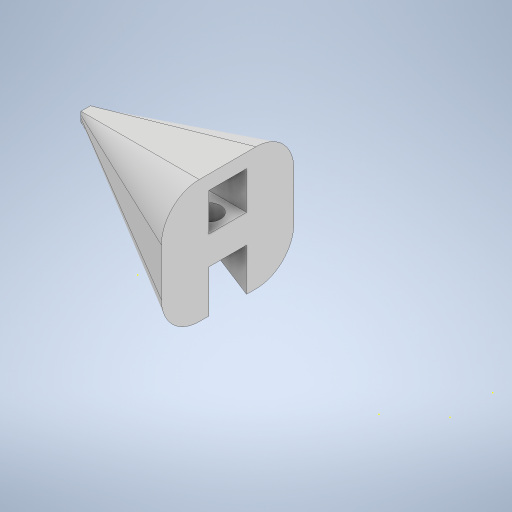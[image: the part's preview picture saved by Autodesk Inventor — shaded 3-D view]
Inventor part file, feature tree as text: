
AUTODESK INVENTOR PART (.ipt)
format: ipt  version: 2024 (Build 280153000, 153)  size: 766,464 bytes
history: native  units: mm
features: sketch x37, extrude x31, move_body x7, plane x5, split x5, boolean_combine x4, chamfer x3, fillet x1, loft x1, other x1
ambient origin geometry x8: Origin, YZ Plane, XZ Plane, XY Plane, X Axis, Y Axis, Z Axis, Center Point
bodies: Solid1 (feature_tree), Solid2 (feature_tree), Solid3 (feature_tree), Solid6 (feature_tree), Solid7 (feature_tree), Solid8 (feature_tree), Solid9 (feature_tree), Solid10 (feature_tree), Solid11 (feature_tree), Solid12 (feature_tree), Solid13 (feature_tree)
feature tree (95):
  extrude  "Extrusion1"  Depth=16.0mm
  sketch  "Sketch2"  dims[d2=15.0mm d3=0.0mm d4=10.0mm]
  extrude  "Extrusion2"  Depth=10.0mm
  chamfer  "Chamfer1"  Distance=21.25mm
  extrude  "Extrusion3"  Depth=10.0mm TaperAngle=0.0deg
  extrude  "Extrusion4"  Depth=11.5mm TaperAngle=0.0deg
  extrude  "Extrusion5"  Depth=1.0mm TaperAngle=0.0deg
  chamfer  "Chamfer2"  Distance=6.0mm Angle=45.0deg
  sketch  "Sketch6"  dims[d14=7.0mm d15=11.5mm d16=0.0mm]
  extrude  "Extrusion6"  Depth=9.0mm
  extrude  "Extrusion7"  Depth=5.5mm TaperAngle=0.0deg
  chamfer  "Chamfer3"  Distance=5.5mm Angle=45.0deg
  sketch  "Sketch9"  dims[d26=3.3mm d27=45.25mm d28=0.0mm d29=11.5mm d30=5.5mm d31=45.0deg]
  extrude  "Extrusion8"  Depth=65.75mm TaperAngle=0.0deg
  extrude  "Extrusion9"  Depth=9.0mm TaperAngle=0.0deg
  extrude  "Extrusion10"  Depth=13.0mm TaperAngle=0.0deg
  sketch  "Sketch13"  dims[d43=24.0mm d44=21.0mm d45=0.0mm]
  extrude  "Extrusion11"  Depth=21.0mm TaperAngle=0.0deg
  extrude  "Extrusion12"  TaperAngle=0.0deg  [1 undecoded]
  extrude  "Extrusion13"  Depth=6.0mm TaperAngle=0.0deg
  plane  "Work Plane1"
  split  "Split1"
  move_body  "Move Body1"
  extrude  "Extrusion14"  Depth=0.5mm TaperAngle=0.0deg
  move_body  "Move Body2"
  extrude  "Extrusion15"  Depth=3.0mm
  sketch  "Sketch19"  dims[d70=31.0mm d71=29.5mm d72=0.0mm]
  sketch  "Sketch20"  dims[d74=11.0mm d75=1.0mm]
  extrude  "Extrusion16"  Depth=10.0mm
  extrude  "Extrusion18"  Depth=29.5mm TaperAngle=0.0deg
  extrude  "Extrusion19"  Depth=1.0mm
  extrude  "Extrusion20"  Depth=10.0mm TaperAngle=0.0deg
  boolean_combine  "Combine1"
  plane  "Work Plane3"
  split  "Split3"
  extrude  "Extrusion21"  TaperAngle=0.0deg  [1 undecoded]
  plane  "Work Plane4"
  split  "Split4"
  move_body  "Move Body3"
  move_body  "Move Body4"
  boolean_combine  "Combine3"
  extrude  "Extrusion22"  Depth=1.0mm TaperAngle=0.0deg
  extrude  "Extrusion23"  Depth=12.5mm TaperAngle=0.0deg
  extrude  "Extrusion24"  TaperAngle=0.0deg  [1 undecoded]
  extrude  "Extrusion25"  Depth=46.5mm TaperAngle=0.0deg
  move_body  "Move Body5"
  sketch  "Sketch32"  dims[d102=46.5mm d103=0.0mm d104=4.0mm d105=1.0mm]
  boolean_combine  "Combine4"
  extrude  "Extrusion26"  Depth=2.0mm
  extrude  "Extrusion27"  Depth=4.0mm
  fillet  "Fillet2"  Radius=1.0mm
  sketch  "Sketch34"  dims[d109=5.5mm d110=4.0mm d111=0.0mm d112=0.0mm]
  extrude  "Extrusion28"  Depth=46.5mm TaperAngle=0.0deg
  plane  "Work Plane5"
  split  "Split5"
  move_body  "Move Body6"
  extrude  "Extrusion29"  Depth=4.0mm TaperAngle=0.0deg
  move_body  "Move Body7"
  boolean_combine  "Combine5"
  extrude  "Extrusion30"  TaperAngle=0.0deg  [1 undecoded]
  plane  "Work Plane6"
  loft  "Loft1"
  split  "Split6"
  extrude  "Extrusion31"  Depth=1.0mm
  extrude  "Extrusion32"  TaperAngle=0.0deg  [1 undecoded]
  sketch  "Sketch1"  dims[d0=36.0mm d1=16.0mm]
  sketch  "Sketch3"  dims[d5=10.0mm]
  sketch  "Sketch4"  dims[d6=3.3mm d7=21.25mm d8=0.0mm]
  sketch  "Sketch5"  dims[d9=10.0mm d10=5.5mm d11=45.0deg d12=10.0mm d13=0.0mm]
  sketch  "Sketch7"  dims[d17=3.3mm d18=1.0mm d19=0.0mm d20=6.0mm d21=11.5mm d22=45.0deg]
  sketch  "Sketch8"  dims[d23=15.0mm d24=0.0mm d25=9.0mm]
  sketch  "Sketch10"  dims[d32=2.0mm d33=65.75mm d34=0.0mm]
  sketch  "Sketch11"  dims[d35=0.5mm d36=0.0mm d37=9.0mm d38=0.0mm]
  sketch  "Sketch12"  dims[d39=0.5mm d40=0.0mm d41=13.0mm d42=0.0mm]
  sketch  "Sketch14"  dims[d46=12.25mm d47=-12.0mm d48=0.0mm d49=0.0mm]
  sketch  "Sketch15"  dims[d50=30.0mm d51=0.0mm d52=6.0mm d53=0.0mm d54=0.0mm]
  sketch  "Sketch16"  dims[d56=0.5mm d57=0.0mm d58=0.5mm d59=0.0mm]
  sketch  "Sketch17"  dims[d64=10.0mm d65=0.0mm d66=3.0mm]
  sketch  "Sketch18"  dims[d67=10.0mm d68=0.0mm d69=1.0mm]
  sketch  "Sketch22"  dims[d76=1.0mm d77=10.0mm d78=0.0mm]
  sketch  "Sketch25"  dims[d79=5.5mm d80=0.0mm d81=0.0mm d82=-1.0mm]
  sketch  "Sketch27"  dims[d83=0.0mm d84=0.0mm d85=1.0mm d86=1.0mm d87=0.0mm]
  sketch  "Sketch28"  dims[d88=1.0mm d89=0.0mm d90=12.5mm d91=0.0mm]
  sketch  "Sketch29"  dims[d92=19.0mm d93=0.0mm d94=-12.0mm d95=0.0mm d96=0.0mm]
  sketch  "Sketch30"  dims[d97=2.0mm d98=46.5mm d99=0.0mm]
  sketch  "Sketch31"  dims[d100=2.0mm d101=2.0mm]
  sketch  "Sketch33"  dims[d106=19.0mm d107=46.5mm d108=0.0mm]
  sketch  "Sketch35"  dims[d113=7.0mm d114=0.0mm d115=-8.0mm d116=0.0mm d117=0.0mm]
  sketch  "Sketch36"  dims[d118=7.0mm d119=19.75mm d120=0.0mm]
  sketch  "Sketch37"  dims[d121=15.0mm d123=1.0mm]
  sketch  "Sketch38"  dims[d124=0.0mm d125=90.0deg d126=0.0mm d127=90.0deg]
  other  "Edges1"
  sketch  "Sketch39"  dims[d128=3.5mm]
  sketch  "Sketch40"  dims[d129=4.0mm]
  sketch  "Sketch41"  dims[d130=4.0mm d131=4.0mm d132=3.0mm d133=4.0mm d134=0.0mm d135=2.5mm d136=4.0mm d137=0.0mm]
note: 5 required parameter values undecoded (feature->parameter linkage not recoverable at this tier; creation-order binding heuristic only, values carry confidence <= 0.55)
